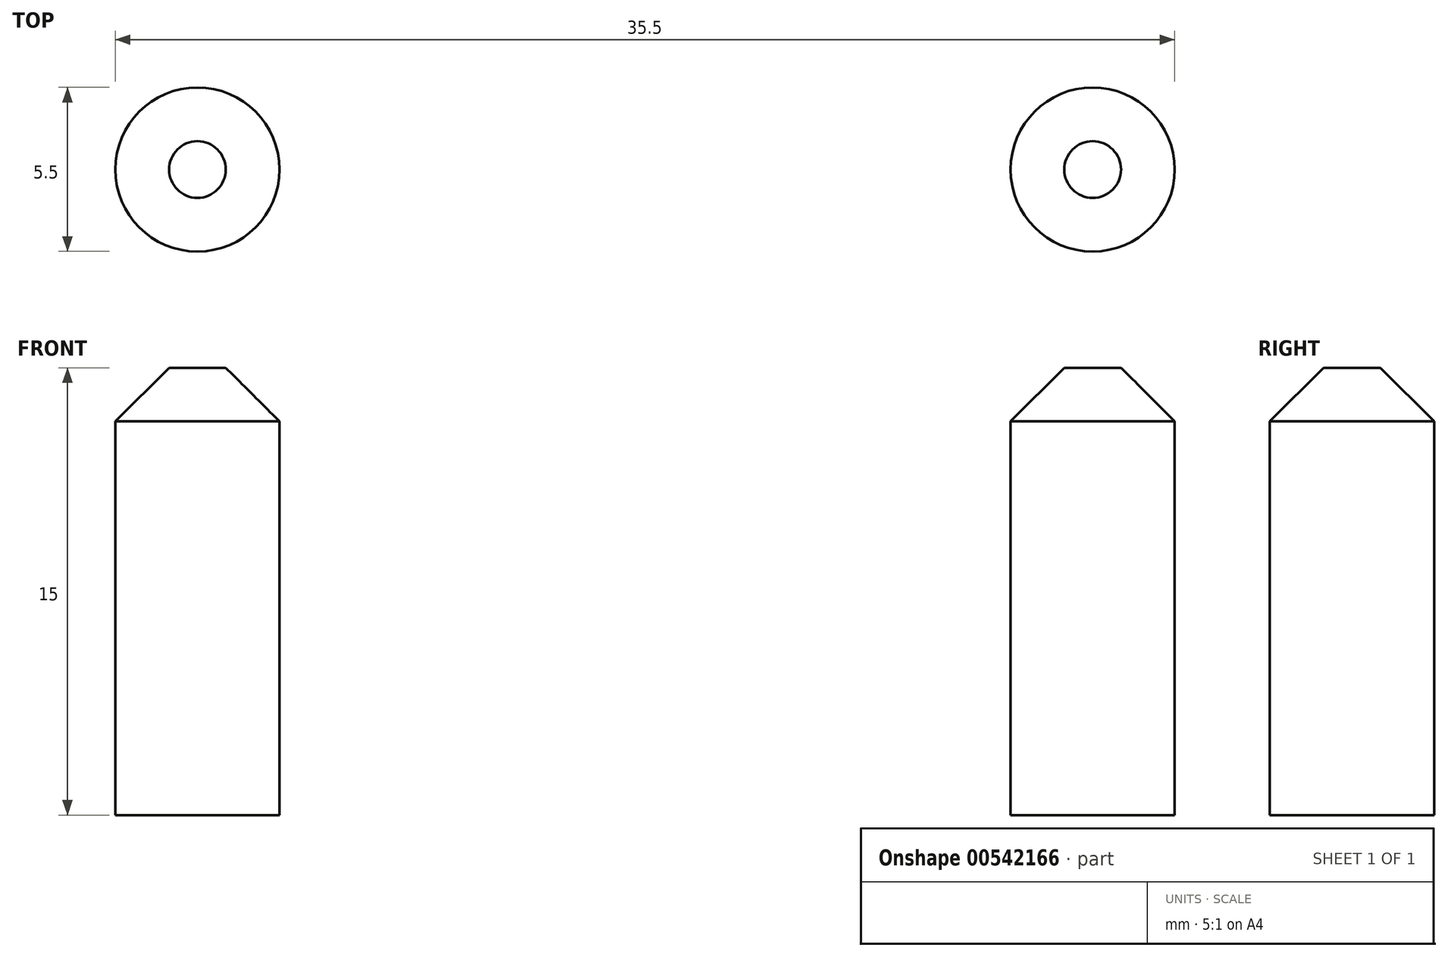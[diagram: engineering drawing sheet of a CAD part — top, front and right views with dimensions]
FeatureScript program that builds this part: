
annotation { "Feature Type Name" : "Feature", "Feature Type Description" : "" }
export const myFeature = defineFeature(function(context is Context, id is Id, definition is map)
    precondition{}
    {
        {
            var Q0;
            Q0=qCreatedBy(makeId("Top.planeOp"),FACE);
            var sketch = newSketch(context, id + "F0", { "sketchPlane" : qUnion([Q0])});
            skLineSegment(sketch, "E0.bottom", {"start": v(-26.46, 49.76) * mm, "end": v(28.54, 49.76) * mm});
            skLineSegment(sketch, "E0.top", {"start": v(-26.46, -50.24) * mm, "end": v(28.54, -50.24) * mm});
            skLineSegment(sketch, "E0.left", {"start": v(-31.46, 44.76) * mm, "end": v(-31.46, -45.24) * mm});
            skLineSegment(sketch, "E0.right", {"start": v(28.54, 49.76) * mm, "end": v(28.54, -50.24) * mm});
            skPoint(sketch, "E1.visualSharp", {"position": v(-31.46, 49.76) * mm});
            skArc(sketch, "E1.filletArc", {"start": v(-26.46, 49.76) * mm, "mid": v(-30, 48.3) * mm, "end": v(-31.46, 44.76) * mm});
            skPoint(sketch, "E2.visualSharp", {"position": v(-31.46, -50.24) * mm});
            skArc(sketch, "E2.filletArc", {"start": v(-31.46, -45.24) * mm, "mid": v(-30, -48.77) * mm, "end": v(-26.46, -50.24) * mm});
            skSolve(sketch);
        }
        {
            var Q0;
            Q0=makeQuery(id+"F0.imprint","IMPRINT",FACE,{"disambiguationData":[TD([[makeQuery(id+"F0.imprint","IMPRINT",EDGE,{"derivedFrom":sQuery(id+"F0.wireOp",EDGE,"E0.bottom")}),-1.0]])]});
            extrude(context, id + "F1", {"entities" : qUnion([Q0]), "depth" : 15 * mm, "offsetDistance" : 25 * mm});
        }
        {
            var Q0;
            Q0=makeQuery(id+"F1.opExtrude","SWEPT_FACE",FACE,{"disambiguationData":[OSD([sQuery(id+"F0.wireOp",EDGE,"E0.right")])]});
            var sketch = newSketch(context, id + "F2", { "sketchPlane" : qUnion([Q0])});
            skLineSegment(sketch, "E3.bottom", {"start": v(-20.24, 15) * mm, "end": v(19.76, 15) * mm});
            skLineSegment(sketch, "E3.top", {"start": v(-20.24, 65) * mm, "end": v(19.76, 65) * mm});
            skLineSegment(sketch, "E3.left", {"start": v(-20.24, 15) * mm, "end": v(-20.24, 65) * mm});
            skLineSegment(sketch, "E3.right", {"start": v(19.76, 15) * mm, "end": v(19.76, 65) * mm});
            skSolve(sketch);
        }
        {
            var Q0;
            Q0=makeQuery(id+"F2.imprint","IMPRINT",FACE,{"disambiguationData":[TD([[makeQuery(id+"F2.imprint","IMPRINT",EDGE,{"derivedFrom":sQuery(id+"F2.wireOp",EDGE,"E3.bottom")}),-1.0]])]});
            extrude(context, id + "F3", {"entities" : qUnion([Q0]), "operationType" : NewBodyOperationType.ADD, "oppositeDirection" : true, "depth" : 15 * mm, "offsetDistance" : 25 * mm, "hasSecondDirection" : true, "secondDirectionOppositeDirection" : false, "secondDirectionDepth" : 0 * mm});
        }
        {
            var Q0;
            Q0=makeQuery(id+"F3.opExtrude","SWEPT_EDGE",EDGE,{"disambiguationData":[OSD([sQuery(id+"F2.wireOp",EDGE,"E3.top"),sQuery(id+"F2.wireOp",EDGE,"E3.right")])]});
            var Q1;
            Q1=makeQuery(id+"F3.opExtrude","SWEPT_EDGE",EDGE,{"disambiguationData":[OSD([sQuery(id+"F2.wireOp",EDGE,"E3.top"),sQuery(id+"F2.wireOp",EDGE,"E3.left")])]});
            var Q2;
            Q2=makeQuery(id+"F3.opExtrude","CAP_EDGE",EDGE,{"disambiguationData":[OSD([sQuery(id+"F2.wireOp",EDGE,"E3.bottom")])],"isStart":false});
            var Q3;
            Q3=makeQuery(id+"F3.opExtrude","SWEPT_EDGE",EDGE,{"disambiguationData":[OSD([sQuery(id+"F0.wireOp",EDGE,"E0.right"),sQuery(id+"F2.wireOp",EDGE,"E3.bottom"),sQuery(id+"F2.wireOp",EDGE,"E3.right")])]});
            var Q4;
            Q4=makeQuery(id+"F3.opExtrude","SWEPT_EDGE",EDGE,{"disambiguationData":[OSD([sQuery(id+"F0.wireOp",EDGE,"E0.right"),sQuery(id+"F2.wireOp",EDGE,"E3.bottom"),sQuery(id+"F2.wireOp",EDGE,"E3.left")])]});
            fillet(context, id + "F4", {"entities" : qUnion([Q0, Q1, Q2, Q3, Q4]), "radius" : 5 * mm, "tangentPropagation" : true, "allowEdgeOverflow" : false});
        }
        {
            var Q0;
            Q0=makeQuery(id+"F3.opExtrude","CAP_FACE",FACE,{"disambiguationData":[OSD([sQuery(id+"F2.wireOp",EDGE,"E3.bottom"),sQuery(id+"F2.wireOp",EDGE,"E3.top"),sQuery(id+"F2.wireOp",EDGE,"E3.left"),sQuery(id+"F2.wireOp",EDGE,"E3.right")])],"isStart":false});
            var sketch = newSketch(context, id + "F5", { "sketchPlane" : qUnion([Q0])});
            skCircle(sketch, "E4", {"center": v(0, 50) * mm, "radius": 7.5 * mm});
            skSolve(sketch);
        }
        {
            var Q0;
            Q0=makeQuery(id+"F5.imprint","IMPRINT",FACE,{"disambiguationData":[TD([[makeQuery(id+"F5.imprint","IMPRINT",EDGE,{"derivedFrom":sQuery(id+"F5.wireOp",EDGE,"E4")}),1.0]])]});
            extrude(context, id + "F6", {"entities" : qUnion([Q0]), "operationType" : NewBodyOperationType.REMOVE, "oppositeDirection" : true, "depth" : 25 * mm, "offsetDistance" : 25 * mm});
        }
        {
            var Q0;
            Q0=makeQuery(id+"F1.opExtrude","CAP_FACE",FACE,{"disambiguationData":[OSD([sQuery(id+"F0.wireOp",EDGE,"E0.bottom"),sQuery(id+"F0.wireOp",EDGE,"E0.top"),sQuery(id+"F0.wireOp",EDGE,"E0.left"),sQuery(id+"F0.wireOp",EDGE,"E0.right"),sQuery(id+"F0.wireOp",EDGE,"E1.filletArc"),sQuery(id+"F0.wireOp",EDGE,"E2.filletArc")])],"isStart":true});
            var sketch = newSketch(context, id + "F7", { "sketchPlane" : qUnion([Q0])});
            skCircle(sketch, "E5", {"center": v(13.54, 30.24) * mm, "radius": 2.75 * mm});
            skCircle(sketch, "E6", {"center": v(-16.46, 30.24) * mm, "radius": 2.75 * mm});
            skCircle(sketch, "E7.MirrorC", {"center": v(-16.46, -30.24) * mm, "radius": 2.75 * mm});
            skCircle(sketch, "E8.MirrorC", {"center": v(13.54, -30.24) * mm, "radius": 2.75 * mm});
            skSolve(sketch);
        }
        {
            var Q0;
            Q0=makeQuery(id+"F7.imprint","IMPRINT",FACE,{"disambiguationData":[TD([[makeQuery(id+"F7.imprint","IMPRINT",EDGE,{"derivedFrom":sQuery(id+"F7.wireOp",EDGE,"E5")}),1.0]])]});
            var Q1;
            Q1=makeQuery(id+"F7.imprint","IMPRINT",FACE,{"disambiguationData":[TD([[makeQuery(id+"F7.imprint","IMPRINT",EDGE,{"derivedFrom":sQuery(id+"F7.wireOp",EDGE,"E6")}),1.0]])]});
            var Q2;
            Q2=makeQuery(id+"F7.imprint","IMPRINT",FACE,{"disambiguationData":[TD([[makeQuery(id+"F7.imprint","IMPRINT",EDGE,{"derivedFrom":sQuery(id+"F7.wireOp",EDGE,"E7.MirrorC")}),-1.0]])]});
            var Q3;
            Q3=makeQuery(id+"F7.imprint","IMPRINT",FACE,{"disambiguationData":[TD([[makeQuery(id+"F7.imprint","IMPRINT",EDGE,{"derivedFrom":sQuery(id+"F7.wireOp",EDGE,"E8.MirrorC")}),-1.0]])]});
            extrude(context, id + "F8", {"entities" : qUnion([Q0, Q1, Q2, Q3]), "operationType" : NewBodyOperationType.REMOVE, "endBound" : BoundingType.THROUGH_ALL, "oppositeDirection" : true, "depth" : 25 * mm, "offsetDistance" : 25 * mm});
        }
        {
            var Q0;
            Q0=makeQuery(id+"F8.boolean.opBoolean","INTERSECT",EDGE,{"derivedFrom":[makeQuery(id+"F1.opExtrude","CAP_FACE",FACE,{"disambiguationData":[OSD([sQuery(id+"F0.wireOp",EDGE,"E0.bottom"),sQuery(id+"F0.wireOp",EDGE,"E0.top"),sQuery(id+"F0.wireOp",EDGE,"E0.left"),sQuery(id+"F0.wireOp",EDGE,"E0.right"),sQuery(id+"F0.wireOp",EDGE,"E1.filletArc"),sQuery(id+"F0.wireOp",EDGE,"E2.filletArc")])],"isStart":false}),makeQuery(id+"F8.opExtrude","SWEPT_FACE",FACE,{"disambiguationData":[OSD([sQuery(id+"F7.wireOp",EDGE,"E5")])]})]});
            var Q1;
            Q1=makeQuery(id+"F8.boolean.opBoolean","INTERSECT",EDGE,{"derivedFrom":[makeQuery(id+"F1.opExtrude","CAP_FACE",FACE,{"disambiguationData":[OSD([sQuery(id+"F0.wireOp",EDGE,"E0.bottom"),sQuery(id+"F0.wireOp",EDGE,"E0.top"),sQuery(id+"F0.wireOp",EDGE,"E0.left"),sQuery(id+"F0.wireOp",EDGE,"E0.right"),sQuery(id+"F0.wireOp",EDGE,"E1.filletArc"),sQuery(id+"F0.wireOp",EDGE,"E2.filletArc")])],"isStart":false}),makeQuery(id+"F8.opExtrude","SWEPT_FACE",FACE,{"disambiguationData":[OSD([sQuery(id+"F7.wireOp",EDGE,"E6")])]})]});
            var Q2;
            Q2=makeQuery(id+"F8.boolean.opBoolean","INTERSECT",EDGE,{"derivedFrom":[makeQuery(id+"F1.opExtrude","CAP_FACE",FACE,{"disambiguationData":[OSD([sQuery(id+"F0.wireOp",EDGE,"E0.bottom"),sQuery(id+"F0.wireOp",EDGE,"E0.top"),sQuery(id+"F0.wireOp",EDGE,"E0.left"),sQuery(id+"F0.wireOp",EDGE,"E0.right"),sQuery(id+"F0.wireOp",EDGE,"E1.filletArc"),sQuery(id+"F0.wireOp",EDGE,"E2.filletArc")])],"isStart":false}),makeQuery(id+"F8.opExtrude","SWEPT_FACE",FACE,{"disambiguationData":[OSD([sQuery(id+"F7.wireOp",EDGE,"E7.MirrorC")])]})]});
            var Q3;
            Q3=makeQuery(id+"F8.boolean.opBoolean","INTERSECT",EDGE,{"derivedFrom":[makeQuery(id+"F1.opExtrude","CAP_FACE",FACE,{"disambiguationData":[OSD([sQuery(id+"F0.wireOp",EDGE,"E0.bottom"),sQuery(id+"F0.wireOp",EDGE,"E0.top"),sQuery(id+"F0.wireOp",EDGE,"E0.left"),sQuery(id+"F0.wireOp",EDGE,"E0.right"),sQuery(id+"F0.wireOp",EDGE,"E1.filletArc"),sQuery(id+"F0.wireOp",EDGE,"E2.filletArc")])],"isStart":false}),makeQuery(id+"F8.opExtrude","SWEPT_FACE",FACE,{"disambiguationData":[OSD([sQuery(id+"F7.wireOp",EDGE,"E8.MirrorC")])]})]});
            chamfer(context, id + "F9", {"entities" : qUnion([Q0, Q1, Q2, Q3]), "width" : 1.8 * mm, "tangentPropagation" : true});
        }
    });
